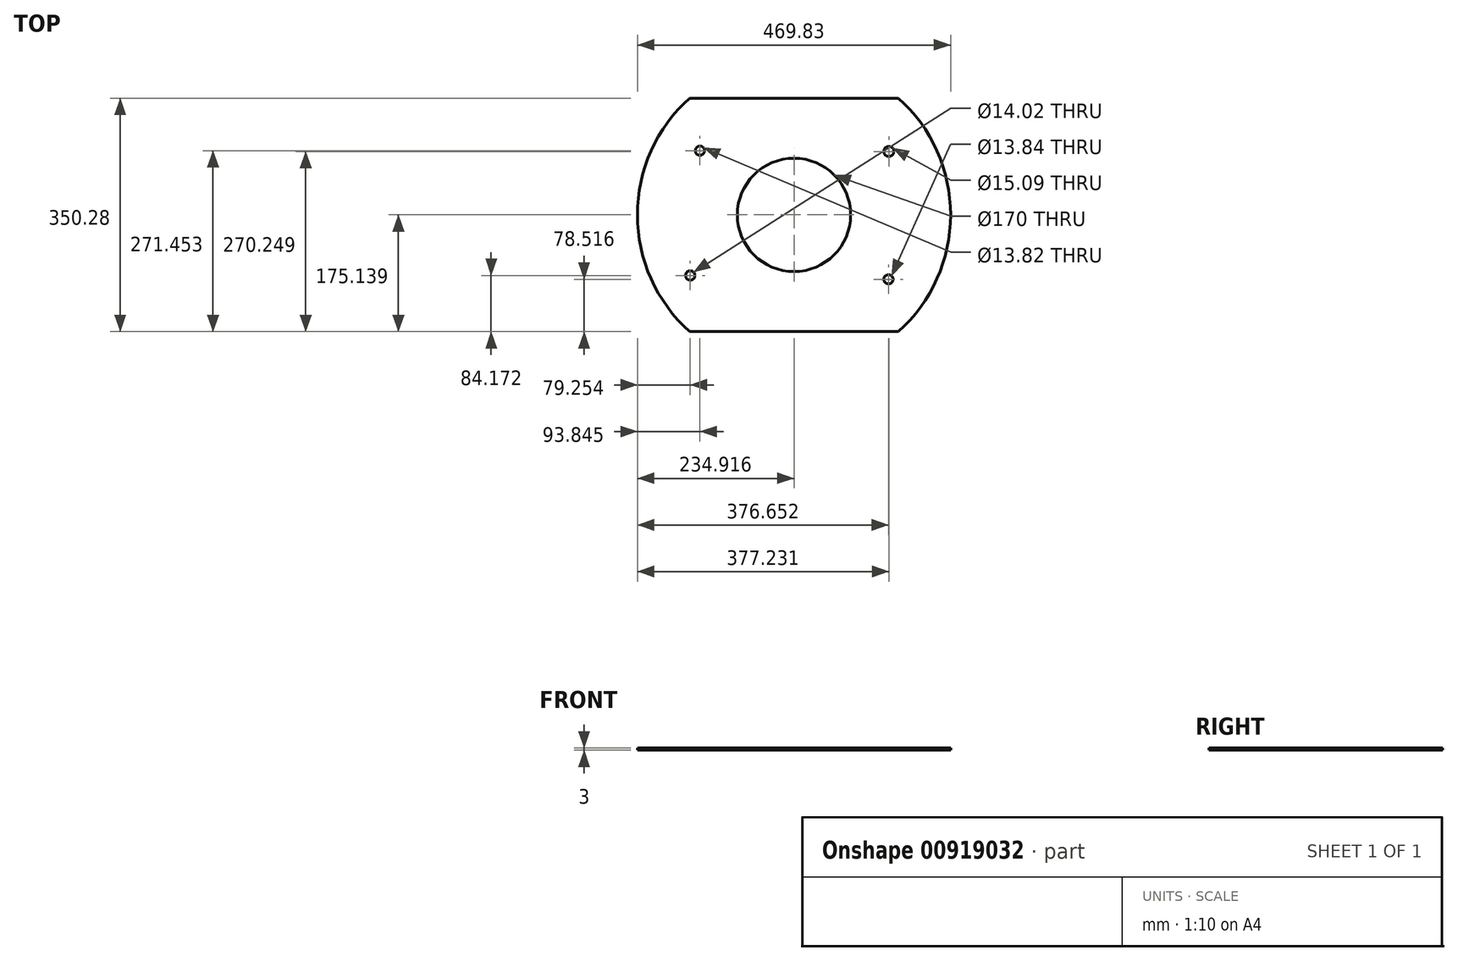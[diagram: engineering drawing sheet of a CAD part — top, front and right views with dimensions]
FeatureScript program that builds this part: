
annotation { "Feature Type Name" : "Feature", "Feature Type Description" : "" }
export const myFeature = defineFeature(function(context is Context, id is Id, definition is map)
    precondition{}
    {
        {
            var Q0;
            Q0=qCreatedBy(makeId("Top.planeOp"),FACE);
            var sketch = newSketch(context, id + "F0", { "sketchPlane" : qUnion([Q0])});
            skLineSegment(sketch, "E0", {"start": v(-158.77, -147.96) * mm, "end": v(-154.5, -152.35) * mm});
            skLineSegment(sketch, "E1", {"start": v(-154.5, -152.35) * mm, "end": v(-152.51, -152.53) * mm});
            skLineSegment(sketch, "E2", {"start": v(151.5, -153.31) * mm, "end": v(154.39, -153.06) * mm});
            skLineSegment(sketch, "E3", {"start": v(154.39, -153.06) * mm, "end": v(158.17, -149.2) * mm});
            skLineSegment(sketch, "E4", {"start": v(158.99, -149.86) * mm, "end": v(155.02, -154) * mm});
            skLineSegment(sketch, "E5", {"start": v(155.02, -154) * mm, "end": v(122.13, -154) * mm});
            skLineSegment(sketch, "E6", {"start": v(44.59, -153.79) * mm, "end": v(44.59, -153.79) * mm});
            skLineSegment(sketch, "E7", {"start": v(-66.83, -70.4) * mm, "end": v(-66.83, -55.46) * mm});
            skLineSegment(sketch, "E8", {"start": v(-66.83, -55.46) * mm, "end": v(-68.23, -53.8) * mm});
            skLineSegment(sketch, "E9", {"start": v(-69.12, 57.2) * mm, "end": v(-66.84, 60.02) * mm});
            skLineSegment(sketch, "E10", {"start": v(-66.84, 60.02) * mm, "end": v(-66.66, 75.23) * mm});
            skLineSegment(sketch, "E11", {"start": v(67.44, 72.4) * mm, "end": v(67.45, 59.42) * mm});
            skLineSegment(sketch, "E12", {"start": v(67.45, 59.42) * mm, "end": v(68.38, 58.55) * mm});
            skLineSegment(sketch, "E13", {"start": v(69.37, -52.77) * mm, "end": v(67.06, -55.7) * mm});
            skLineSegment(sketch, "E14", {"start": v(67.06, -55.7) * mm, "end": v(67.1, -70.3) * mm});
            skLineSegment(sketch, "E15", {"start": v(-48.47, -97.3) * mm, "end": v(-48.47, -97.3) * mm});
            skLineSegment(sketch, "E16", {"start": v(67.43, 58.04) * mm, "end": v(66.42, 59.12) * mm});
            skLineSegment(sketch, "E17", {"start": v(66.42, 59.12) * mm, "end": v(66.3, 74.42) * mm});
            skLineSegment(sketch, "E18", {"start": v(66.3, 74.42) * mm, "end": v(66.19, 89.72) * mm});
            skLineSegment(sketch, "E19", {"start": v(66.19, 89.72) * mm, "end": v(65.15, 91.97) * mm});
            skLineSegment(sketch, "E20", {"start": v(-65.75, 73.8) * mm, "end": v(-65.75, 59.65) * mm});
            skLineSegment(sketch, "E21", {"start": v(-65.75, 59.65) * mm, "end": v(-67.84, 57.04) * mm});
            skLineSegment(sketch, "E22", {"start": v(-159.56, -89.44) * mm, "end": v(-158.1, -89.5) * mm});
            skLineSegment(sketch, "E23", {"start": v(-158.1, -89.5) * mm, "end": v(-159.71, -89.73) * mm});
            skFitSpline(sketch, "E24", {"points": [v(44.59, -153.79) * mm, v(20.04, -153.67) * mm, v(-34.6, -153.55) * mm, v(-76.83, -153.52) * mm]});
            skFitSpline(sketch, "E25", {"points": [v(-76.83, -153.52) * mm, v(-140.66, -153.47) * mm, v(-153.81, -153.38) * mm, v(-154.79, -152.98) * mm]});
            skFitSpline(sketch, "E26", {"points": [v(-154.79, -152.98) * mm, v(-155.87, -152.52) * mm, v(-163.77, -144.52) * mm, v(-166.1, -141.52) * mm]});
            skFitSpline(sketch, "E27", {"points": [v(-166.1, -141.52) * mm, v(-166.64, -140.82) * mm, v(-168.72, -138.23) * mm, v(-170.71, -135.78) * mm]});
            skFitSpline(sketch, "E28", {"points": [v(-170.71, -135.78) * mm, v(-179.67, -124.75) * mm, v(-185.63, -115.93) * mm, v(-192.42, -103.68) * mm]});
            skFitSpline(sketch, "E29", {"points": [v(-192.42, -103.68) * mm, v(-204.28, -82.26) * mm, v(-211.62, -61.65) * mm, v(-216.38, -36.46) * mm]});
            skFitSpline(sketch, "E30", {"points": [v(-216.38, -36.46) * mm, v(-217.29, -31.66) * mm, v(-217.57, -29.6) * mm, v(-218.57, -20.44) * mm]});
            skFitSpline(sketch, "E31", {"points": [v(-218.57, -20.44) * mm, v(-220.9, 0.8) * mm, v(-219.77, 25.42) * mm, v(-215.48, 46.88) * mm]});
            skFitSpline(sketch, "E32", {"points": [v(-215.48, 46.88) * mm, v(-212.67, 60.96) * mm, v(-207.35, 77.93) * mm, v(-202.01, 89.9) * mm]});
            skFitSpline(sketch, "E33", {"points": [v(-202.01, 89.9) * mm, v(-201.35, 91.38) * mm, v(-200.41, 93.49) * mm, v(-199.93, 94.58) * mm]});
            skFitSpline(sketch, "E34", {"points": [v(-199.93, 94.58) * mm, v(-195.35, 104.83) * mm, v(-187.95, 117.86) * mm, v(-181.24, 127.48) * mm]});
            skFitSpline(sketch, "E35", {"points": [v(-181.24, 127.48) * mm, v(-179.6, 129.84) * mm, v(-177.74, 132.5) * mm, v(-177.1, 133.42) * mm]});
            skFitSpline(sketch, "E36", {"points": [v(-177.1, 133.42) * mm, v(-176.48, 134.33) * mm, v(-175.76, 135.3) * mm, v(-175.51, 135.58) * mm]});
            skFitSpline(sketch, "E37", {"points": [v(-175.51, 135.58) * mm, v(-175.26, 135.86) * mm, v(-173.96, 137.54) * mm, v(-172.6, 139.33) * mm]});
            skFitSpline(sketch, "E38", {"points": [v(-172.6, 139.33) * mm, v(-171.26, 141.1) * mm, v(-169.83, 142.8) * mm, v(-169.43, 143.07) * mm]});
            skFitSpline(sketch, "E39", {"points": [v(-169.43, 143.07) * mm, v(-168.68, 143.6) * mm, v(-168.4, 144.5) * mm, v(-169.13, 144.04) * mm]});
            skFitSpline(sketch, "E40", {"points": [v(-169.13, 144.04) * mm, v(-169.39, 143.88) * mm, v(-169.44, 143.94) * mm, v(-169.28, 144.2) * mm]});
            skFitSpline(sketch, "E41", {"points": [v(-169.28, 144.2) * mm, v(-169.14, 144.44) * mm, v(-168.88, 144.54) * mm, v(-168.7, 144.43) * mm]});
            skFitSpline(sketch, "E42", {"points": [v(-168.7, 144.43) * mm, v(-168.53, 144.32) * mm, v(-168.1, 144.68) * mm, v(-167.75, 145.23) * mm]});
            skFitSpline(sketch, "E43", {"points": [v(-167.75, 145.23) * mm, v(-166.97, 146.48) * mm, v(-166.35, 147.22) * mm, v(-164.75, 148.82) * mm]});
            skFitSpline(sketch, "E44", {"points": [v(-164.75, 148.82) * mm, v(-164.06, 149.5) * mm, v(-163.53, 150.23) * mm, v(-163.59, 150.43) * mm]});
            skFitSpline(sketch, "E45", {"points": [v(-163.59, 150.43) * mm, v(-163.64, 150.63) * mm, v(-163.53, 150.7) * mm, v(-163.33, 150.57) * mm]});
            skFitSpline(sketch, "E46", {"points": [v(-163.33, 150.57) * mm, v(-163.14, 150.45) * mm, v(-162.37, 151.17) * mm, v(-161.63, 152.16) * mm]});
            skFitSpline(sketch, "E47", {"points": [v(-161.63, 152.16) * mm, v(-160.68, 153.44) * mm, v(-160.03, 153.98) * mm, v(-159.43, 153.98) * mm]});
            skFitSpline(sketch, "E48", {"points": [v(-159.43, 153.98) * mm, v(-158.36, 153.98) * mm, v(-158.43, 153.86) * mm, v(-161.98, 150.14) * mm]});
            skFitSpline(sketch, "E49", {"points": [v(-161.98, 150.14) * mm, v(-163.58, 148.46) * mm, v(-165.14, 146.73) * mm, v(-165.44, 146.3) * mm]});
            skFitSpline(sketch, "E50", {"points": [v(-165.44, 146.3) * mm, v(-165.73, 145.87) * mm, v(-167.52, 143.65) * mm, v(-169.41, 141.37) * mm]});
            skFitSpline(sketch, "E51", {"points": [v(-169.41, 141.37) * mm, v(-171.3, 139.1) * mm, v(-173.57, 136.26) * mm, v(-174.46, 135.07) * mm]});
            skFitSpline(sketch, "E52", {"points": [v(-174.46, 135.07) * mm, v(-175.34, 133.89) * mm, v(-176.2, 132.75) * mm, v(-176.35, 132.56) * mm]});
            skFitSpline(sketch, "E53", {"points": [v(-176.35, 132.56) * mm, v(-178.97, 129.3) * mm, v(-186.94, 116.97) * mm, v(-191.22, 109.52) * mm]});
            skFitSpline(sketch, "E54", {"points": [v(-191.22, 109.52) * mm, v(-202.62, 89.66) * mm, v(-211.97, 63.16) * mm, v(-215.86, 39.68) * mm]});
            skFitSpline(sketch, "E55", {"points": [v(-215.86, 39.68) * mm, v(-219.82, 15.76) * mm, v(-219.68, -14.45) * mm, v(-215.5, -35.92) * mm]});
            skFitSpline(sketch, "E56", {"points": [v(-215.5, -35.92) * mm, v(-215.35, -36.72) * mm, v(-214.97, -38.74) * mm, v(-214.66, -40.42) * mm]});
            skFitSpline(sketch, "E57", {"points": [v(-214.66, -40.42) * mm, v(-212.88, -50) * mm, v(-207.62, -67.85) * mm, v(-203.63, -77.86) * mm]});
            skFitSpline(sketch, "E58", {"points": [v(-203.63, -77.86) * mm, v(-196.86, -94.81) * mm, v(-186.42, -113.45) * mm, v(-175.6, -127.9) * mm]});
            skFitSpline(sketch, "E59", {"points": [v(-175.6, -127.9) * mm, v(-170.94, -134.11) * mm, v(-162.77, -143.86) * mm, v(-158.77, -147.96) * mm]});
            skFitSpline(sketch, "E60", {"points": [v(-152.51, -152.53) * mm, v(-151.42, -152.63) * mm, v(-87.6, -152.8) * mm, v(-10.67, -152.91) * mm]});
            skFitSpline(sketch, "E61", {"points": [v(-10.67, -152.91) * mm, v(66.25, -153.02) * mm, v(133.56, -153.21) * mm, v(138.9, -153.34) * mm]});
            skFitSpline(sketch, "E62", {"points": [v(138.9, -153.34) * mm, v(144.26, -153.47) * mm, v(149.93, -153.46) * mm, v(151.5, -153.31) * mm]});
            skFitSpline(sketch, "E63", {"points": [v(158.17, -149.2) * mm, v(171.85, -135.25) * mm, v(186.95, -114) * mm, v(195.38, -96.84) * mm]});
            skFitSpline(sketch, "E64", {"points": [v(195.38, -96.84) * mm, v(206.59, -74.03) * mm, v(213.5, -52.17) * mm, v(216.67, -29.5) * mm]});
            skFitSpline(sketch, "E65", {"points": [v(216.67, -29.5) * mm, v(218.46, -16.68) * mm, v(218.78, -11.86) * mm, v(218.8, 2.42) * mm]});
            skFitSpline(sketch, "E66", {"points": [v(218.8, 2.42) * mm, v(218.81, 12.95) * mm, v(218.68, 17.26) * mm, v(218.17, 22.04) * mm]});
            skFitSpline(sketch, "E67", {"points": [v(218.17, 22.04) * mm, v(216.47, 38.25) * mm, v(213.8, 51.98) * mm, v(209.83, 65.05) * mm]});
            skFitSpline(sketch, "E68", {"points": [v(209.83, 65.05) * mm, v(208.18, 70.46) * mm, v(205.5, 78.4) * mm, v(204.97, 79.42) * mm]});
            skFitSpline(sketch, "E69", {"points": [v(204.97, 79.42) * mm, v(204.8, 79.73) * mm, v(204.4, 80.8) * mm, v(204.05, 81.8) * mm]});
            skFitSpline(sketch, "E70", {"points": [v(204.05, 81.8) * mm, v(203.7, 82.79) * mm, v(202.88, 84.78) * mm, v(202.22, 86.23) * mm]});
            skFitSpline(sketch, "E71", {"points": [v(202.22, 86.23) * mm, v(201.55, 87.68) * mm, v(201, 88.95) * mm, v(201, 89.06) * mm]});
            skFitSpline(sketch, "E72", {"points": [v(201, 89.06) * mm, v(201, 89.32) * mm, v(197.35, 97.26) * mm, v(195.3, 101.42) * mm]});
            skFitSpline(sketch, "E73", {"points": [v(195.3, 101.42) * mm, v(193.27, 105.57) * mm, v(188.66, 113.76) * mm, v(187.47, 115.34) * mm]});
            skFitSpline(sketch, "E74", {"points": [v(187.47, 115.34) * mm, v(187, 115.97) * mm, v(186.6, 116.57) * mm, v(186.6, 116.68) * mm]});
            skFitSpline(sketch, "E75", {"points": [v(186.6, 116.68) * mm, v(186.6, 117.07) * mm, v(182.91, 122.72) * mm, v(178.41, 129.2) * mm]});
            skFitSpline(sketch, "E76", {"points": [v(178.41, 129.2) * mm, v(173.94, 135.64) * mm, v(164.9, 146.79) * mm, v(161.08, 150.55) * mm]});
            skFitSpline(sketch, "E77", {"points": [v(161.08, 150.55) * mm, v(159.48, 152.13) * mm, v(158.17, 153.54) * mm, v(158.17, 153.7) * mm]});
            skFitSpline(sketch, "E78", {"points": [v(158.17, 153.7) * mm, v(158.17, 154.35) * mm, v(159.74, 153.9) * mm, v(160.65, 152.99) * mm]});
            skFitSpline(sketch, "E79", {"points": [v(160.65, 152.99) * mm, v(163.2, 150.41) * mm, v(166.83, 146.25) * mm, v(170.34, 141.9) * mm]});
            skFitSpline(sketch, "E80", {"points": [v(170.34, 141.9) * mm, v(176.5, 134.25) * mm, v(177.44, 133.03) * mm, v(178.79, 130.92) * mm]});
            skFitSpline(sketch, "E81", {"points": [v(178.79, 130.92) * mm, v(179.49, 129.82) * mm, v(180.32, 128.7) * mm, v(180.63, 128.45) * mm]});
            skFitSpline(sketch, "E82", {"points": [v(180.63, 128.45) * mm, v(180.95, 128.18) * mm, v(181.2, 127.81) * mm, v(181.2, 127.62) * mm]});
            skFitSpline(sketch, "E83", {"points": [v(181.2, 127.62) * mm, v(181.2, 127.43) * mm, v(181.78, 126.51) * mm, v(182.48, 125.6) * mm]});
            skFitSpline(sketch, "E84", {"points": [v(182.48, 125.6) * mm, v(183.98, 123.61) * mm, v(188.05, 117.4) * mm, v(188.05, 117.08) * mm]});
            skFitSpline(sketch, "E85", {"points": [v(188.05, 117.08) * mm, v(188.05, 116.96) * mm, v(188.72, 115.86) * mm, v(189.54, 114.63) * mm]});
            skFitSpline(sketch, "E86", {"points": [v(189.54, 114.63) * mm, v(191.13, 112.24) * mm, v(196.77, 101.25) * mm, v(198.83, 96.53) * mm]});
            skFitSpline(sketch, "E87", {"points": [v(198.83, 96.53) * mm, v(199.52, 94.96) * mm, v(200.75, 92.22) * mm, v(201.56, 90.44) * mm]});
            skFitSpline(sketch, "E88", {"points": [v(201.56, 90.44) * mm, v(202.38, 88.65) * mm, v(203.34, 86.47) * mm, v(203.7, 85.58) * mm]});
            skFitSpline(sketch, "E89", {"points": [v(203.7, 85.58) * mm, v(204.06, 84.68) * mm, v(204.57, 83.44) * mm, v(204.84, 82.82) * mm]});
            skFitSpline(sketch, "E90", {"points": [v(204.84, 82.82) * mm, v(205.1, 82.2) * mm, v(205.33, 81.46) * mm, v(205.33, 81.18) * mm]});
            skFitSpline(sketch, "E91", {"points": [v(205.33, 81.18) * mm, v(205.33, 80.9) * mm, v(205.48, 80.53) * mm, v(205.66, 80.34) * mm]});
            skFitSpline(sketch, "E92", {"points": [v(205.66, 80.34) * mm, v(205.83, 80.15) * mm, v(206.88, 77.32) * mm, v(207.98, 74.06) * mm]});
            skFitSpline(sketch, "E93", {"points": [v(207.98, 74.06) * mm, v(214.3, 55.25) * mm, v(217.55, 39.5) * mm, v(219.38, 18.8) * mm]});
            skFitSpline(sketch, "E94", {"points": [v(219.38, 18.8) * mm, v(219.87, 13.33) * mm, v(219.87, -6.17) * mm, v(219.39, -13.14) * mm]});
            skFitSpline(sketch, "E95", {"points": [v(219.39, -13.14) * mm, v(217.23, -44.28) * mm, v(208.41, -74.87) * mm, v(193.73, -102.16) * mm]});
            skFitSpline(sketch, "E96", {"points": [v(193.73, -102.16) * mm, v(184.56, -119.22) * mm, v(172.55, -135.71) * mm, v(158.99, -149.86) * mm]});
            skFitSpline(sketch, "E97", {"points": [v(122.13, -154) * mm, v(104.03, -154) * mm, v(69.14, -153.9) * mm, v(44.59, -153.79) * mm]});
            skFitSpline(sketch, "E98", {"points": [v(-132.8, -152.15) * mm, v(-132.56, -152.05) * mm, v(-132.08, -152.04) * mm, v(-131.73, -152.14) * mm]});
            skFitSpline(sketch, "E99", {"points": [v(-131.73, -152.14) * mm, v(-131.38, -152.23) * mm, v(-131.58, -152.3) * mm, v(-132.17, -152.31) * mm]});
            skFitSpline(sketch, "E100", {"points": [v(-132.17, -152.31) * mm, v(-132.76, -152.32) * mm, v(-133.05, -152.25) * mm, v(-132.8, -152.15) * mm]});
            skFitSpline(sketch, "E101", {"points": [v(142.69, -101.62) * mm, v(142.69, -101.1) * mm, v(142.93, -100.9) * mm, v(143.6, -100.9) * mm]});
            skFitSpline(sketch, "E102", {"points": [v(143.6, -100.9) * mm, v(144.1, -100.9) * mm, v(145.39, -100.4) * mm, v(146.48, -99.8) * mm]});
            skFitSpline(sketch, "E103", {"points": [v(146.48, -99.8) * mm, v(147.56, -99.18) * mm, v(148.45, -98.85) * mm, v(148.45, -99.06) * mm]});
            skFitSpline(sketch, "E104", {"points": [v(148.45, -99.06) * mm, v(148.45, -99.56) * mm, v(145.11, -101.26) * mm, v(144.14, -101.26) * mm]});
            skFitSpline(sketch, "E105", {"points": [v(144.14, -101.26) * mm, v(143.74, -101.26) * mm, v(143.4, -101.43) * mm, v(143.4, -101.62) * mm]});
            skFitSpline(sketch, "E106", {"points": [v(143.4, -101.62) * mm, v(143.4, -102.28) * mm, v(144.55, -102) * mm, v(146.52, -100.88) * mm]});
            skFitSpline(sketch, "E107", {"points": [v(146.52, -100.88) * mm, v(147.59, -100.27) * mm, v(148.66, -99.83) * mm, v(148.9, -99.92) * mm]});
            skFitSpline(sketch, "E108", {"points": [v(148.9, -99.92) * mm, v(149.15, -100) * mm, v(148.46, -100.58) * mm, v(147.37, -101.2) * mm]});
            skFitSpline(sketch, "E109", {"points": [v(147.37, -101.2) * mm, v(144.98, -102.57) * mm, v(142.69, -102.78) * mm, v(142.69, -101.62) * mm]});
            skFitSpline(sketch, "E110", {"points": [v(137.6, -98.15) * mm, v(133.77, -97.67) * mm, v(133.36, -91.62) * mm, v(136.96, -88.54) * mm]});
            skFitSpline(sketch, "E111", {"points": [v(136.96, -88.54) * mm, v(137.73, -87.88) * mm, v(138.37, -87.07) * mm, v(138.37, -86.74) * mm]});
            skFitSpline(sketch, "E112", {"points": [v(138.37, -86.74) * mm, v(138.37, -86.38) * mm, v(138.66, -86.14) * mm, v(139.09, -86.14) * mm]});
            skFitSpline(sketch, "E113", {"points": [v(139.09, -86.14) * mm, v(139.49, -86.14) * mm, v(139.8, -86.35) * mm, v(139.8, -86.6) * mm]});
            skFitSpline(sketch, "E114", {"points": [v(139.8, -86.6) * mm, v(139.8, -86.92) * mm, v(140.25, -87.02) * mm, v(141.23, -86.93) * mm]});
            skFitSpline(sketch, "E115", {"points": [v(141.23, -86.93) * mm, v(144.18, -86.65) * mm, v(147.72, -88.89) * mm, v(148.44, -91.5) * mm]});
            skFitSpline(sketch, "E116", {"points": [v(148.44, -91.5) * mm, v(149.2, -94.2) * mm, v(148.6, -97.25) * mm, v(147.23, -97.78) * mm]});
            skFitSpline(sketch, "E117", {"points": [v(147.23, -97.78) * mm, v(146.49, -98.06) * mm, v(139.18, -98.34) * mm, v(137.6, -98.15) * mm]});
            skFitSpline(sketch, "E118", {"points": [v(145.66, -96.8) * mm, v(145.85, -96.52) * mm, v(146.02, -96.55) * mm, v(146.24, -96.9) * mm]});
            skFitSpline(sketch, "E119", {"points": [v(146.24, -96.9) * mm, v(146.83, -97.8) * mm, v(147.49, -95.95) * mm, v(147.52, -93.32) * mm]});
            skFitSpline(sketch, "E120", {"points": [v(147.52, -93.32) * mm, v(147.58, -89.34) * mm, v(143.1, -86.76) * mm, v(139.05, -88.45) * mm]});
            skFitSpline(sketch, "E121", {"points": [v(139.05, -88.45) * mm, v(137.66, -89.03) * mm, v(136.92, -89.77) * mm, v(136.08, -91.42) * mm]});
            skFitSpline(sketch, "E122", {"points": [v(136.08, -91.42) * mm, v(135.5, -92.59) * mm, v(135.37, -95.14) * mm, v(135.9, -95.14) * mm]});
            skFitSpline(sketch, "E123", {"points": [v(135.9, -95.14) * mm, v(136.07, -95.14) * mm, v(136.2, -95.54) * mm, v(136.2, -96.02) * mm]});
            skFitSpline(sketch, "E124", {"points": [v(136.2, -96.02) * mm, v(136.2, -96.5) * mm, v(136.37, -97) * mm, v(136.57, -97.12) * mm]});
            skFitSpline(sketch, "E125", {"points": [v(136.57, -97.12) * mm, v(136.77, -97.25) * mm, v(136.93, -97.06) * mm, v(136.93, -96.72) * mm]});
            skFitSpline(sketch, "E126", {"points": [v(136.93, -96.72) * mm, v(136.93, -96.13) * mm, v(136.97, -96.14) * mm, v(137.42, -96.75) * mm]});
            skFitSpline(sketch, "E127", {"points": [v(137.42, -96.75) * mm, v(137.68, -97.12) * mm, v(138.05, -97.32) * mm, v(138.23, -97.2) * mm]});
            skFitSpline(sketch, "E128", {"points": [v(138.23, -97.2) * mm, v(138.42, -97.1) * mm, v(139.13, -97.12) * mm, v(139.82, -97.26) * mm]});
            skFitSpline(sketch, "E129", {"points": [v(139.82, -97.26) * mm, v(141.5, -97.6) * mm, v(145.32, -97.3) * mm, v(145.66, -96.8) * mm]});
            skFitSpline(sketch, "E130", {"points": [v(-48.47, -97.3) * mm, v(-56.8, -96.95) * mm, v(-59.86, -96.3) * mm, v(-61.86, -94.5) * mm]});
            skFitSpline(sketch, "E131", {"points": [v(-61.86, -94.5) * mm, v(-63.94, -92.62) * mm, v(-65.2, -90.6) * mm, v(-66.07, -87.81) * mm]});
            skFitSpline(sketch, "E132", {"points": [v(-66.07, -87.81) * mm, v(-66.8, -85.47) * mm, v(-66.83, -84.6) * mm, v(-66.83, -70.4) * mm]});
            skFitSpline(sketch, "E133", {"points": [v(-68.23, -53.8) * mm, v(-81.54, -37.86) * mm, v(-89.18, -15.51) * mm, v(-88.3, 4.94) * mm]});
            skFitSpline(sketch, "E134", {"points": [v(-88.3, 4.94) * mm, v(-87.46, 24.43) * mm, v(-80.7, 42.86) * mm, v(-69.12, 57.2) * mm]});
            skFitSpline(sketch, "E135", {"points": [v(-66.66, 75.23) * mm, v(-66.52, 87.88) * mm, v(-66.4, 90.77) * mm, v(-65.9, 92.42) * mm]});
            skFitSpline(sketch, "E136", {"points": [v(-65.9, 92.42) * mm, v(-64.15, 98.32) * mm, v(-59.37, 102.95) * mm, v(-53.7, 104.25) * mm]});
            skFitSpline(sketch, "E137", {"points": [v(-53.7, 104.25) * mm, v(-51.2, 104.82) * mm, v(-52.44, 104.8) * mm, v(2.1, 104.72) * mm]});
            skFitSpline(sketch, "E138", {"points": [v(2.1, 104.72) * mm, v(55.94, 104.63) * mm, v(53.66, 104.72) * mm, v(57.72, 102.43) * mm]});
            skFitSpline(sketch, "E139", {"points": [v(57.72, 102.43) * mm, v(60.55, 100.83) * mm, v(63.19, 98.75) * mm, v(64.11, 97.36) * mm]});
            skFitSpline(sketch, "E140", {"points": [v(64.11, 97.36) * mm, v(65.6, 95.16) * mm, v(66.78, 91.65) * mm, v(67.11, 88.48) * mm]});
            skFitSpline(sketch, "E141", {"points": [v(67.11, 88.48) * mm, v(67.3, 86.78) * mm, v(67.44, 79.55) * mm, v(67.44, 72.4) * mm]});
            skFitSpline(sketch, "E142", {"points": [v(68.38, 58.55) * mm, v(68.9, 58.07) * mm, v(70.4, 56.14) * mm, v(71.73, 54.26) * mm]});
            skFitSpline(sketch, "E143", {"points": [v(71.73, 54.26) * mm, v(82.98, 38.3) * mm, v(88.44, 21.38) * mm, v(88.42, 2.6) * mm]});
            skFitSpline(sketch, "E144", {"points": [v(88.42, 2.6) * mm, v(88.41, -7.6) * mm, v(87.29, -15.27) * mm, v(84.53, -23.86) * mm]});
            skFitSpline(sketch, "E145", {"points": [v(84.53, -23.86) * mm, v(83.8, -26.14) * mm, v(82.97, -28.76) * mm, v(82.69, -29.69) * mm]});
            skFitSpline(sketch, "E146", {"points": [v(82.69, -29.69) * mm, v(81.79, -32.63) * mm, v(76.92, -42.04) * mm, v(74.25, -46) * mm]});
            skFitSpline(sketch, "E147", {"points": [v(74.25, -46) * mm, v(72.84, -48.1) * mm, v(70.64, -51.15) * mm, v(69.37, -52.77) * mm]});
            skFitSpline(sketch, "E148", {"points": [v(67.1, -70.3) * mm, v(67.13, -79.3) * mm, v(67.01, -85.5) * mm, v(66.78, -86.5) * mm]});
            skFitSpline(sketch, "E149", {"points": [v(66.78, -86.5) * mm, v(65.94, -90.15) * mm, v(63.73, -93.8) * mm, v(61.31, -95.52) * mm]});
            skFitSpline(sketch, "E150", {"points": [v(61.31, -95.52) * mm, v(58.68, -97.4) * mm, v(58.16, -97.41) * mm, v(6.25, -97.5) * mm]});
            skFitSpline(sketch, "E151", {"points": [v(6.25, -97.5) * mm, v(-20.18, -97.53) * mm, v(-44.8, -97.44) * mm, v(-48.47, -97.3) * mm]});
            skFitSpline(sketch, "E152", {"points": [v(50.61, -95.73) * mm, v(52.34, -95.61) * mm, v(54.09, -95.31) * mm, v(54.5, -95.06) * mm]});
            skFitSpline(sketch, "E153", {"points": [v(54.5, -95.06) * mm, v(55.1, -94.68) * mm, v(55.29, -94.7) * mm, v(55.58, -95.14) * mm]});
            skFitSpline(sketch, "E154", {"points": [v(55.58, -95.14) * mm, v(55.87, -95.6) * mm, v(55.92, -95.6) * mm, v(55.92, -95.05) * mm]});
            skFitSpline(sketch, "E155", {"points": [v(55.92, -95.05) * mm, v(55.93, -94.57) * mm, v(56.23, -94.42) * mm, v(57.23, -94.42) * mm]});
            skFitSpline(sketch, "E156", {"points": [v(57.23, -94.42) * mm, v(58.35, -94.42) * mm, v(58.47, -94.5) * mm, v(58.09, -94.96) * mm]});
            skFitSpline(sketch, "E157", {"points": [v(58.09, -94.96) * mm, v(57.39, -95.81) * mm, v(58.55, -95.67) * mm, v(59.33, -94.8) * mm]});
            skFitSpline(sketch, "E158", {"points": [v(59.33, -94.8) * mm, v(59.67, -94.43) * mm, v(60.17, -94.2) * mm, v(60.44, -94.3) * mm]});
            skFitSpline(sketch, "E159", {"points": [v(60.44, -94.3) * mm, v(60.7, -94.4) * mm, v(61.2, -94.03) * mm, v(61.57, -93.46) * mm]});
            skFitSpline(sketch, "E160", {"points": [v(61.57, -93.46) * mm, v(61.93, -92.9) * mm, v(62.65, -92.09) * mm, v(63.17, -91.65) * mm]});
            skFitSpline(sketch, "E161", {"points": [v(63.17, -91.65) * mm, v(64.21, -90.76) * mm, v(65.92, -86.36) * mm, v(66, -84.34) * mm]});
            skFitSpline(sketch, "E162", {"points": [v(66, -84.34) * mm, v(66.03, -83.65) * mm, v(66.14, -76.6) * mm, v(66.24, -68.68) * mm]});
            skFitSpline(sketch, "E163", {"points": [v(66.24, -68.68) * mm, v(66.4, -56.92) * mm, v(66.52, -54.18) * mm, v(66.94, -53.72) * mm]});
            skFitSpline(sketch, "E164", {"points": [v(66.94, -53.72) * mm, v(67.22, -53.4) * mm, v(67.45, -53) * mm, v(67.45, -52.81) * mm]});
            skFitSpline(sketch, "E165", {"points": [v(67.45, -52.81) * mm, v(67.45, -52.63) * mm, v(68.17, -51.67) * mm, v(69.06, -50.68) * mm]});
            skFitSpline(sketch, "E166", {"points": [v(69.06, -50.68) * mm, v(69.94, -49.7) * mm, v(70.87, -48.48) * mm, v(71.13, -47.98) * mm]});
            skFitSpline(sketch, "E167", {"points": [v(71.13, -47.98) * mm, v(71.38, -47.49) * mm, v(71.96, -46.68) * mm, v(72.42, -46.18) * mm]});
            skFitSpline(sketch, "E168", {"points": [v(72.42, -46.18) * mm, v(72.87, -45.69) * mm, v(73.53, -44.8) * mm, v(73.89, -44.2) * mm]});
            skFitSpline(sketch, "E169", {"points": [v(73.89, -44.2) * mm, v(75.84, -40.94) * mm, v(76.6, -39.49) * mm, v(76.5, -39.18) * mm]});
            skFitSpline(sketch, "E170", {"points": [v(76.5, -39.18) * mm, v(76.45, -38.99) * mm, v(76.62, -38.66) * mm, v(76.89, -38.46) * mm]});
            skFitSpline(sketch, "E171", {"points": [v(76.89, -38.46) * mm, v(77.36, -38.1) * mm, v(78.17, -36.52) * mm, v(80.23, -31.96) * mm]});
            skFitSpline(sketch, "E172", {"points": [v(80.23, -31.96) * mm, v(80.77, -30.78) * mm, v(81.36, -29.51) * mm, v(81.54, -29.16) * mm]});
            skFitSpline(sketch, "E173", {"points": [v(81.54, -29.16) * mm, v(81.72, -28.8) * mm, v(81.78, -28.36) * mm, v(81.66, -28.17) * mm]});
            skFitSpline(sketch, "E174", {"points": [v(81.66, -28.17) * mm, v(81.54, -27.98) * mm, v(81.6, -27.82) * mm, v(81.79, -27.82) * mm]});
            skFitSpline(sketch, "E175", {"points": [v(81.79, -27.82) * mm, v(81.97, -27.82) * mm, v(82.21, -27.54) * mm, v(82.32, -27.2) * mm]});
            skFitSpline(sketch, "E176", {"points": [v(82.32, -27.2) * mm, v(82.42, -26.85) * mm, v(82.85, -25.63) * mm, v(83.26, -24.49) * mm]});
            skFitSpline(sketch, "E177", {"points": [v(83.26, -24.49) * mm, v(85.66, -17.9) * mm, v(87.2, -9.1) * mm, v(87.5, -0.1) * mm]});
            skFitSpline(sketch, "E178", {"points": [v(87.5, -0.1) * mm, v(88.13, 19.1) * mm, v(82.14, 38.18) * mm, v(70.4, 54.26) * mm]});
            skFitSpline(sketch, "E179", {"points": [v(70.4, 54.26) * mm, v(69.32, 55.74) * mm, v(67.98, 57.44) * mm, v(67.43, 58.04) * mm]});
            skFitSpline(sketch, "E180", {"points": [v(65.15, 91.97) * mm, v(64.58, 93.2) * mm, v(64, 94.22) * mm, v(63.87, 94.22) * mm]});
            skFitSpline(sketch, "E181", {"points": [v(63.87, 94.22) * mm, v(63.73, 94.22) * mm, v(63.36, 94.74) * mm, v(63.05, 95.39) * mm]});
            skFitSpline(sketch, "E182", {"points": [v(63.05, 95.39) * mm, v(60.89, 99.78) * mm, v(55.01, 103.45) * mm, v(49.9, 103.59) * mm]});
            skFitSpline(sketch, "E183", {"points": [v(49.9, 103.59) * mm, v(48.77, 103.62) * mm, v(32.28, 103.63) * mm, v(13.27, 103.6) * mm]});
            skFitSpline(sketch, "E184", {"points": [v(13.27, 103.6) * mm, v(-5.74, 103.58) * mm, v(-27.53, 103.67) * mm, v(-35.15, 103.8) * mm]});
            skFitSpline(sketch, "E185", {"points": [v(-35.15, 103.8) * mm, v(-45.07, 103.97) * mm, v(-49.77, 103.91) * mm, v(-51.7, 103.6) * mm]});
            skFitSpline(sketch, "E186", {"points": [v(-51.7, 103.6) * mm, v(-54.47, 103.17) * mm, v(-58.03, 101.65) * mm, v(-59.63, 100.22) * mm]});
            skFitSpline(sketch, "E187", {"points": [v(-59.63, 100.22) * mm, v(-61.27, 98.76) * mm, v(-62.89, 96.7) * mm, v(-62.68, 96.35) * mm]});
            skFitSpline(sketch, "E188", {"points": [v(-62.68, 96.35) * mm, v(-62.56, 96.17) * mm, v(-62.63, 96.02) * mm, v(-62.84, 96.02) * mm]});
            skFitSpline(sketch, "E189", {"points": [v(-62.84, 96.02) * mm, v(-63.4, 96.02) * mm, v(-64.93, 92.42) * mm, v(-65.36, 90.06) * mm]});
            skFitSpline(sketch, "E190", {"points": [v(-65.36, 90.06) * mm, v(-65.6, 88.8) * mm, v(-65.75, 82.37) * mm, v(-65.75, 73.8) * mm]});
            skFitSpline(sketch, "E191", {"points": [v(-67.84, 57.04) * mm, v(-70.71, 53.48) * mm, v(-72.89, 50.34) * mm, v(-75.08, 46.6) * mm]});
            skFitSpline(sketch, "E192", {"points": [v(-75.08, 46.6) * mm, v(-76.9, 43.53) * mm, v(-80.29, 36.6) * mm, v(-81.2, 34.1) * mm]});
            skFitSpline(sketch, "E193", {"points": [v(-81.2, 34.1) * mm, v(-81.46, 33.4) * mm, v(-81.8, 32.51) * mm, v(-81.96, 32.12) * mm]});
            skFitSpline(sketch, "E194", {"points": [v(-81.96, 32.12) * mm, v(-83.53, 28.37) * mm, v(-85.42, 21.06) * mm, v(-86.51, 14.48) * mm]});
            skFitSpline(sketch, "E195", {"points": [v(-86.51, 14.48) * mm, v(-87.43, 8.98) * mm, v(-87.42, -5.2) * mm, v(-86.5, -10.18) * mm]});
            skFitSpline(sketch, "E196", {"points": [v(-86.5, -10.18) * mm, v(-85.01, -18.32) * mm, v(-82.78, -26.1) * mm, v(-80.81, -30.06) * mm]});
            skFitSpline(sketch, "E197", {"points": [v(-80.81, -30.06) * mm, v(-80.25, -31.2) * mm, v(-79.8, -32.3) * mm, v(-79.8, -32.51) * mm]});
            skFitSpline(sketch, "E198", {"points": [v(-79.8, -32.51) * mm, v(-79.8, -32.73) * mm, v(-79.39, -33.5) * mm, v(-78.9, -34.23) * mm]});
            skFitSpline(sketch, "E199", {"points": [v(-78.9, -34.23) * mm, v(-78.4, -34.96) * mm, v(-78, -35.75) * mm, v(-78, -36) * mm]});
            skFitSpline(sketch, "E200", {"points": [v(-78, -36) * mm, v(-78, -36.25) * mm, v(-77.32, -37.55) * mm, v(-76.5, -38.89) * mm]});
            skFitSpline(sketch, "E201", {"points": [v(-76.5, -38.89) * mm, v(-75.67, -40.23) * mm, v(-74.78, -41.81) * mm, v(-74.5, -42.4) * mm]});
            skFitSpline(sketch, "E202", {"points": [v(-74.5, -42.4) * mm, v(-74.24, -43) * mm, v(-73.45, -44.21) * mm, v(-72.75, -45.1) * mm]});
            skFitSpline(sketch, "E203", {"points": [v(-72.75, -45.1) * mm, v(-72.06, -46) * mm, v(-71.4, -47) * mm, v(-71.28, -47.35) * mm]});
            skFitSpline(sketch, "E204", {"points": [v(-71.28, -47.35) * mm, v(-71.16, -47.7) * mm, v(-70.92, -47.98) * mm, v(-70.75, -47.98) * mm]});
            skFitSpline(sketch, "E205", {"points": [v(-70.75, -47.98) * mm, v(-70.57, -47.98) * mm, v(-70.43, -48.23) * mm, v(-70.43, -48.52) * mm]});
            skFitSpline(sketch, "E206", {"points": [v(-70.43, -48.52) * mm, v(-70.43, -48.82) * mm, v(-70.27, -49.06) * mm, v(-70.08, -49.06) * mm]});
            skFitSpline(sketch, "E207", {"points": [v(-70.08, -49.06) * mm, v(-69.89, -49.06) * mm, v(-69.49, -49.54) * mm, v(-69.19, -50.11) * mm]});
            skFitSpline(sketch, "E208", {"points": [v(-69.19, -50.11) * mm, v(-68.9, -50.69) * mm, v(-68.43, -51.37) * mm, v(-68.16, -51.64) * mm]});
            skFitSpline(sketch, "E209", {"points": [v(-68.16, -51.64) * mm, v(-67.9, -51.9) * mm, v(-67.37, -52.6) * mm, v(-66.99, -53.19) * mm]});
            skFitSpline(sketch, "E210", {"points": [v(-66.99, -53.19) * mm, v(-66.33, -54.18) * mm, v(-66.28, -55.22) * mm, v(-66.1, -69.75) * mm]});
            skFitSpline(sketch, "E211", {"points": [v(-66.1, -69.75) * mm, v(-65.92, -83.04) * mm, v(-65.8, -85.5) * mm, v(-65.28, -87.04) * mm]});
            skFitSpline(sketch, "E212", {"points": [v(-65.28, -87.04) * mm, v(-64.55, -89.2) * mm, v(-62.22, -92.65) * mm, v(-61.13, -93.2) * mm]});
            skFitSpline(sketch, "E213", {"points": [v(-61.13, -93.2) * mm, v(-60.7, -93.41) * mm, v(-60.02, -93.89) * mm, v(-59.62, -94.26) * mm]});
            skFitSpline(sketch, "E214", {"points": [v(-59.62, -94.26) * mm, v(-58.92, -94.89) * mm, v(-58.9, -94.9) * mm, v(-59.13, -94.27) * mm]});
            skFitSpline(sketch, "E215", {"points": [v(-59.13, -94.27) * mm, v(-59.33, -93.75) * mm, v(-59.24, -93.66) * mm, v(-58.7, -93.82) * mm]});
            skFitSpline(sketch, "E216", {"points": [v(-58.7, -93.82) * mm, v(-58.32, -93.93) * mm, v(-57.08, -94.21) * mm, v(-55.94, -94.46) * mm]});
            skFitSpline(sketch, "E217", {"points": [v(-55.94, -94.46) * mm, v(-54.8, -94.7) * mm, v(-53.87, -95.02) * mm, v(-53.87, -95.16) * mm]});
            skFitSpline(sketch, "E218", {"points": [v(-53.87, -95.16) * mm, v(-53.87, -95.53) * mm, v(-54.39, -95.51) * mm, v(-34.43, -95.8) * mm]});
            skFitSpline(sketch, "E219", {"points": [v(-34.43, -95.8) * mm, v(-14.07, -96.08) * mm, v(45.9, -96.03) * mm, v(50.61, -95.73) * mm]});
            skFitSpline(sketch, "E220", {"points": [v(-159.53, -91.73) * mm, v(-159.73, -91.66) * mm, v(-160.3, -91.52) * mm, v(-160.82, -91.4) * mm]});
            skFitSpline(sketch, "E221", {"points": [v(-160.82, -91.4) * mm, v(-162, -91.15) * mm, v(-162.6, -89.86) * mm, v(-162.6, -87.56) * mm]});
            skFitSpline(sketch, "E222", {"points": [v(-162.6, -87.56) * mm, v(-162.6, -83.13) * mm, v(-159.39, -80.38) * mm, v(-154.8, -80.85) * mm]});
            skFitSpline(sketch, "E223", {"points": [v(-154.8, -80.85) * mm, v(-151.08, -81.24) * mm, v(-148.65, -83.98) * mm, v(-148.58, -87.87) * mm]});
            skFitSpline(sketch, "E224", {"points": [v(-148.58, -87.87) * mm, v(-148.54, -90.01) * mm, v(-149.33, -91.4) * mm, v(-150.74, -91.68) * mm]});
            skFitSpline(sketch, "E225", {"points": [v(-150.74, -91.68) * mm, v(-151.9, -91.9) * mm, v(-158.87, -91.95) * mm, v(-159.53, -91.73) * mm]});
            skFitSpline(sketch, "E226", {"points": [v(-154.5, -90.47) * mm, v(-153.85, -90.22) * mm, v(-153.36, -90.24) * mm, v(-152.89, -90.54) * mm]});
            skFitSpline(sketch, "E227", {"points": [v(-152.89, -90.54) * mm, v(-152.35, -90.87) * mm, v(-151.98, -90.86) * mm, v(-151.19, -90.49) * mm]});
            skFitSpline(sketch, "E228", {"points": [v(-151.19, -90.49) * mm, v(-150.6, -90.2) * mm, v(-150.36, -89.94) * mm, v(-150.63, -89.85) * mm]});
            skFitSpline(sketch, "E229", {"points": [v(-150.63, -89.85) * mm, v(-150.93, -89.73) * mm, v(-150.8, -89.46) * mm, v(-150.22, -89) * mm]});
            skFitSpline(sketch, "E230", {"points": [v(-150.22, -89) * mm, v(-148.11, -87.34) * mm, v(-150.7, -82.8) * mm, v(-154.33, -81.82) * mm]});
            skFitSpline(sketch, "E231", {"points": [v(-154.33, -81.82) * mm, v(-157.3, -81.02) * mm, v(-160.6, -82.96) * mm, v(-161.53, -86.08) * mm]});
            skFitSpline(sketch, "E232", {"points": [v(-161.53, -86.08) * mm, v(-162.2, -88.28) * mm, v(-161.56, -89.37) * mm, v(-159.56, -89.44) * mm]});
            skFitSpline(sketch, "E233", {"points": [v(-159.71, -89.73) * mm, v(-161.57, -90) * mm, v(-161.09, -90.38) * mm, v(-158.63, -90.57) * mm]});
            skFitSpline(sketch, "E234", {"points": [v(-158.63, -90.57) * mm, v(-157.74, -90.64) * mm, v(-156.66, -90.73) * mm, v(-156.22, -90.76) * mm]});
            skFitSpline(sketch, "E235", {"points": [v(-156.22, -90.76) * mm, v(-155.8, -90.8) * mm, v(-155.02, -90.66) * mm, v(-154.5, -90.47) * mm]});
            skFitSpline(sketch, "E236", {"points": [v(138.7, 94.36) * mm, v(138.62, 94.44) * mm, v(138, 94.6) * mm, v(137.35, 94.7) * mm]});
            skFitSpline(sketch, "E237", {"points": [v(137.35, 94.7) * mm, v(135.22, 95.03) * mm, v(134.45, 96.79) * mm, v(135.05, 100) * mm]});
            skFitSpline(sketch, "E238", {"points": [v(135.05, 100) * mm, v(135.48, 102.33) * mm, v(136.45, 103.67) * mm, v(138.45, 104.7) * mm]});
            skFitSpline(sketch, "E239", {"points": [v(138.45, 104.7) * mm, v(140.19, 105.58) * mm, v(143.86, 105.58) * mm, v(145.39, 104.7) * mm]});
            skFitSpline(sketch, "E240", {"points": [v(145.39, 104.7) * mm, v(147.85, 103.25) * mm, v(149.46, 99.33) * mm, v(148.47, 97.17) * mm]});
            skFitSpline(sketch, "E241", {"points": [v(148.47, 97.17) * mm, v(147.39, 94.81) * mm, v(147.16, 94.44) * mm, v(146.73, 94.3) * mm]});
            skFitSpline(sketch, "E242", {"points": [v(146.73, 94.3) * mm, v(146.45, 94.2) * mm, v(146.57, 94.64) * mm, v(147.02, 95.41) * mm]});
            skFitSpline(sketch, "E243", {"points": [v(147.02, 95.41) * mm, v(147.44, 96.12) * mm, v(147.61, 96.76) * mm, v(147.42, 96.88) * mm]});
            skFitSpline(sketch, "E244", {"points": [v(147.42, 96.88) * mm, v(147.24, 97) * mm, v(147, 96.85) * mm, v(146.88, 96.55) * mm]});
            skFitSpline(sketch, "E245", {"points": [v(146.88, 96.55) * mm, v(146.76, 96.25) * mm, v(146.24, 96.02) * mm, v(145.67, 96.03) * mm]});
            skFitSpline(sketch, "E246", {"points": [v(145.67, 96.03) * mm, v(144.7, 96.04) * mm, v(144.7, 96.05) * mm, v(145.39, 96.58) * mm]});
            skFitSpline(sketch, "E247", {"points": [v(145.39, 96.58) * mm, v(145.79, 96.88) * mm, v(146.1, 97.32) * mm, v(146.1, 97.56) * mm]});
            skFitSpline(sketch, "E248", {"points": [v(146.1, 97.56) * mm, v(146.1, 97.8) * mm, v(146.47, 98.05) * mm, v(146.92, 98.11) * mm]});
            skFitSpline(sketch, "E249", {"points": [v(146.92, 98.11) * mm, v(147.5, 98.2) * mm, v(147.73, 98.47) * mm, v(147.73, 99.08) * mm]});
            skFitSpline(sketch, "E250", {"points": [v(147.73, 99.08) * mm, v(147.73, 99.55) * mm, v(147.57, 100.03) * mm, v(147.37, 100.16) * mm]});
            skFitSpline(sketch, "E251", {"points": [v(147.37, 100.16) * mm, v(147.17, 100.28) * mm, v(147, 100.64) * mm, v(147, 100.96) * mm]});
            skFitSpline(sketch, "E252", {"points": [v(147, 100.96) * mm, v(147, 101.27) * mm, v(146.77, 101.8) * mm, v(146.49, 102.1) * mm]});
            skFitSpline(sketch, "E253", {"points": [v(146.49, 102.1) * mm, v(146.2, 102.42) * mm, v(145.64, 103.03) * mm, v(145.25, 103.46) * mm]});
            skFitSpline(sketch, "E254", {"points": [v(145.25, 103.46) * mm, v(144.16, 104.67) * mm, v(141.63, 104.91) * mm, v(139.54, 104) * mm]});
            skFitSpline(sketch, "E255", {"points": [v(139.54, 104) * mm, v(137.36, 103.06) * mm, v(135.59, 100.78) * mm, v(136.18, 99.68) * mm]});
            skFitSpline(sketch, "E256", {"points": [v(136.18, 99.68) * mm, v(136.44, 99.2) * mm, v(136.45, 98.86) * mm, v(136.21, 98.72) * mm]});
            skFitSpline(sketch, "E257", {"points": [v(136.21, 98.72) * mm, v(135.62, 98.35) * mm, v(135.8, 97.62) * mm, v(136.73, 96.6) * mm]});
            skFitSpline(sketch, "E258", {"points": [v(136.73, 96.6) * mm, v(137.56, 95.71) * mm, v(139.03, 95.23) * mm, v(138.55, 96.02) * mm]});
            skFitSpline(sketch, "E259", {"points": [v(138.55, 96.02) * mm, v(138.43, 96.21) * mm, v(138.5, 96.38) * mm, v(138.7, 96.38) * mm]});
            skFitSpline(sketch, "E260", {"points": [v(138.7, 96.38) * mm, v(138.92, 96.38) * mm, v(139.09, 96.15) * mm, v(139.09, 95.87) * mm]});
            skFitSpline(sketch, "E261", {"points": [v(139.09, 95.87) * mm, v(139.09, 94.98) * mm, v(141.2, 94.83) * mm, v(144.26, 95.52) * mm]});
            skFitSpline(sketch, "E262", {"points": [v(144.26, 95.52) * mm, v(145.22, 95.74) * mm, v(145.26, 95.7) * mm, v(144.88, 94.98) * mm]});
            skFitSpline(sketch, "E263", {"points": [v(144.88, 94.98) * mm, v(144.5, 94.3) * mm, v(144.16, 94.22) * mm, v(141.66, 94.22) * mm]});
            skFitSpline(sketch, "E264", {"points": [v(141.66, 94.22) * mm, v(140.11, 94.22) * mm, v(138.78, 94.28) * mm, v(138.7, 94.36) * mm]});
            skFitSpline(sketch, "E265", {"points": [v(-146.3, 95.53) * mm, v(-148.48, 96) * mm, v(-148.8, 100.73) * mm, v(-146.82, 103.18) * mm]});
            skFitSpline(sketch, "E266", {"points": [v(-146.82, 103.18) * mm, v(-145.16, 105.23) * mm, v(-143.7, 105.91) * mm, v(-140.93, 105.91) * mm]});
            skFitSpline(sketch, "E267", {"points": [v(-140.93, 105.91) * mm, v(-138.85, 105.92) * mm, v(-138.33, 105.77) * mm, v(-136.97, 104.83) * mm]});
            skFitSpline(sketch, "E268", {"points": [v(-136.97, 104.83) * mm, v(-136.11, 104.23) * mm, v(-135.13, 103.17) * mm, v(-134.78, 102.49) * mm]});
            skFitSpline(sketch, "E269", {"points": [v(-134.78, 102.49) * mm, v(-133.9, 100.74) * mm, v(-133.93, 97.44) * mm, v(-134.84, 96.33) * mm]});
            skFitSpline(sketch, "E270", {"points": [v(-134.84, 96.33) * mm, v(-135.5, 95.51) * mm, v(-135.74, 95.47) * mm, v(-140.5, 95.42) * mm]});
            skFitSpline(sketch, "E271", {"points": [v(-140.5, 95.42) * mm, v(-143.25, 95.39) * mm, v(-145.86, 95.44) * mm, v(-146.3, 95.53) * mm]});
            skFitSpline(sketch, "E272", {"points": [v(-139.33, 96.39) * mm, v(-138.65, 96.65) * mm, v(-138.28, 96.65) * mm, v(-138.12, 96.39) * mm]});
            skFitSpline(sketch, "E273", {"points": [v(-138.12, 96.39) * mm, v(-137.97, 96.14) * mm, v(-137.66, 96.19) * mm, v(-137.2, 96.52) * mm]});
            skFitSpline(sketch, "E274", {"points": [v(-137.2, 96.52) * mm, v(-136.83, 96.8) * mm, v(-136.31, 96.93) * mm, v(-136.06, 96.84) * mm]});
            skFitSpline(sketch, "E275", {"points": [v(-136.06, 96.84) * mm, v(-135.8, 96.74) * mm, v(-135.6, 96.84) * mm, v(-135.6, 97.06) * mm]});
            skFitSpline(sketch, "E276", {"points": [v(-135.6, 97.06) * mm, v(-135.6, 97.28) * mm, v(-135.95, 97.47) * mm, v(-136.4, 97.5) * mm]});
            skFitSpline(sketch, "E277", {"points": [v(-136.4, 97.5) * mm, v(-137.13, 97.53) * mm, v(-137.14, 97.56) * mm, v(-136.5, 97.71) * mm]});
            skFitSpline(sketch, "E278", {"points": [v(-136.5, 97.71) * mm, v(-135.5, 97.95) * mm, v(-135.23, 98.26) * mm, v(-135.03, 99.38) * mm]});
            skFitSpline(sketch, "E279", {"points": [v(-135.03, 99.38) * mm, v(-134.78, 100.73) * mm, v(-136.05, 103.01) * mm, v(-137.65, 104.1) * mm]});
            skFitSpline(sketch, "E280", {"points": [v(-137.65, 104.1) * mm, v(-138.4, 104.6) * mm, v(-139.16, 105.01) * mm, v(-139.36, 105) * mm]});
            skFitSpline(sketch, "E281", {"points": [v(-139.36, 105) * mm, v(-139.57, 105) * mm, v(-139.49, 104.85) * mm, v(-139.2, 104.66) * mm]});
            skFitSpline(sketch, "E282", {"points": [v(-139.2, 104.66) * mm, v(-138.72, 104.35) * mm, v(-138.73, 104.3) * mm, v(-139.26, 104.3) * mm]});
            skFitSpline(sketch, "E283", {"points": [v(-139.26, 104.3) * mm, v(-139.6, 104.3) * mm, v(-139.97, 104.46) * mm, v(-140.1, 104.66) * mm]});
            skFitSpline(sketch, "E284", {"points": [v(-140.1, 104.66) * mm, v(-140.21, 104.85) * mm, v(-140.8, 105.02) * mm, v(-141.38, 105.02) * mm]});
            skFitSpline(sketch, "E285", {"points": [v(-141.38, 105.02) * mm, v(-144.34, 105.02) * mm, v(-147.11, 102.34) * mm, v(-147.11, 99.49) * mm]});
            skFitSpline(sketch, "E286", {"points": [v(-147.11, 99.49) * mm, v(-147.11, 98.36) * mm, v(-146.99, 98.2) * mm, v(-145.94, 97.97) * mm]});
            skFitSpline(sketch, "E287", {"points": [v(-145.94, 97.97) * mm, v(-144.93, 97.75) * mm, v(-144.87, 97.68) * mm, v(-145.5, 97.45) * mm]});
            skFitSpline(sketch, "E288", {"points": [v(-145.5, 97.45) * mm, v(-145.89, 97.3) * mm, v(-146.37, 97.28) * mm, v(-146.57, 97.39) * mm]});
            skFitSpline(sketch, "E289", {"points": [v(-146.57, 97.39) * mm, v(-146.77, 97.5) * mm, v(-146.72, 97.34) * mm, v(-146.47, 97.02) * mm]});
            skFitSpline(sketch, "E290", {"points": [v(-146.47, 97.02) * mm, v(-146.16, 96.65) * mm, v(-145.5, 96.48) * mm, v(-144.49, 96.52) * mm]});
            skFitSpline(sketch, "E291", {"points": [v(-144.49, 96.52) * mm, v(-143.65, 96.56) * mm, v(-142.57, 96.47) * mm, v(-142.07, 96.33) * mm]});
            skFitSpline(sketch, "E292", {"points": [v(-142.07, 96.33) * mm, v(-140.77, 95.96) * mm, v(-140.43, 95.97) * mm, v(-139.33, 96.39) * mm]});
            skFitSpline(sketch, "E293", {"points": [v(139.99, 95.66) * mm, v(139.87, 95.85) * mm, v(139.94, 96.02) * mm, v(140.15, 96.02) * mm]});
            skFitSpline(sketch, "E294", {"points": [v(140.15, 96.02) * mm, v(140.36, 96.02) * mm, v(140.53, 95.85) * mm, v(140.53, 95.66) * mm]});
            skFitSpline(sketch, "E295", {"points": [v(140.53, 95.66) * mm, v(140.53, 95.46) * mm, v(140.46, 95.3) * mm, v(140.37, 95.3) * mm]});
            skFitSpline(sketch, "E296", {"points": [v(140.37, 95.3) * mm, v(140.28, 95.3) * mm, v(140.11, 95.46) * mm, v(139.99, 95.66) * mm]});
            skSolve(sketch);
        }
        {
            var Q0;
            Q0=qCreatedBy(makeId("Top.planeOp"),FACE);
            var sketch = newSketch(context, id + "F1", { "sketchPlane" : qUnion([Q0])});
            skPoint(sketch, "E297.0", {"position": v(-172.6, 139.33) * mm});
            skPoint(sketch, "E298.0", {"position": v(-218.57, -20.44) * mm});
            skPoint(sketch, "E299.0", {"position": v(219.39, -13.14) * mm});
            skCircle(sketch, "E300", {"center": v(0.08, 3.15) * mm, "radius": 219.92 * mm});
            skCircle(sketch, "E301", {"center": v(0.08, 3.15) * mm, "radius": 85 * mm});
            skCircle(sketch, "E302", {"center": v(0.08, 3.15) * mm, "radius": 234.92 * mm});
            skPoint(sketch, "E303.0", {"position": v(-134.78, 102.49) * mm});
            skPoint(sketch, "E304.0", {"position": v(-146.82, 103.18) * mm});
            skPoint(sketch, "E305.0", {"position": v(-134.84, 96.33) * mm});
            skCircle(sketch, "E306", {"center": v(-141, 99.46) * mm, "radius": 6.91 * mm});
            skPoint(sketch, "E307.0", {"position": v(-154.8, -80.85) * mm});
            skPoint(sketch, "E308.0", {"position": v(-148.58, -87.87) * mm});
            skPoint(sketch, "E309.0", {"position": v(-162.6, -87.56) * mm});
            skCircle(sketch, "E310", {"center": v(-155.59, -87.82) * mm, "radius": 7 * mm});
            skPoint(sketch, "E311.0", {"position": v(148.44, -91.5) * mm});
            skPoint(sketch, "E312.0", {"position": v(136.96, -88.54) * mm});
            skPoint(sketch, "E313.0", {"position": v(147.23, -97.78) * mm});
            skCircle(sketch, "E314", {"center": v(141.81, -93.47) * mm, "radius": 6.92 * mm});
            skPoint(sketch, "E315.0", {"position": v(138.45, 104.7) * mm});
            skPoint(sketch, "E316.0", {"position": v(145.39, 104.7) * mm});
            skPoint(sketch, "E317.0", {"position": v(135.05, 100) * mm});
            skCircle(sketch, "E318", {"center": v(142.4, 98.26) * mm, "radius": 7.55 * mm});
            skPoint(sketch, "E318.first.point", {"position": v(146.33, 104.7) * mm});
            skLineSegment(sketch, "E319", {"start": v(-156.48, -172) * mm, "end": v(156.64, -172) * mm});
            skLineSegment(sketch, "E320", {"start": v(0.08, 3.15) * mm, "end": v(-266.63, 3.15) * mm, "construction": true});
            skLineSegment(sketch, "E321.MirrorCS", {"start": v(-156.48, 178.3) * mm, "end": v(156.64, 178.3) * mm});
            skSolve(sketch);
        }
        {
            var Q0;
            {var subQ0=sQuery(id+"F1.wireOp",EDGE,"E321.MirrorCS");var subQ1=sQuery(id+"F1.wireOp",EDGE,"E300");var subQ2=makeQuery(id+"F1.imprint","INTERSECT",VERTEX,{"disambiguationData":[OD(0.0)],"derivedFrom":[subQ1,subQ0]});Q0=makeQuery(id+"F1.imprint","IMPRINT",FACE,{"disambiguationData":[TD([[makeQuery(id+"F1.imprint","IMPRINT",EDGE,{"disambiguationData":[TD([[subQ2,-1.0]])],"derivedFrom":subQ1}),-1.0]])]});}
            var Q1;
            {var subQ0=sQuery(id+"F1.wireOp",EDGE,"E321.MirrorCS");var subQ1=sQuery(id+"F1.wireOp",EDGE,"E300");var subQ2=makeQuery(id+"F1.imprint","INTERSECT",VERTEX,{"disambiguationData":[OD(1.0)],"derivedFrom":[subQ1,subQ0]});Q1=makeQuery(id+"F1.imprint","IMPRINT",FACE,{"disambiguationData":[TD([[makeQuery(id+"F1.imprint","IMPRINT",EDGE,{"disambiguationData":[TD([[subQ2,1.0]])],"derivedFrom":subQ1}),-1.0]])]});}
            var Q2;
            Q2=makeQuery(id+"F1.imprint","IMPRINT",FACE,{"disambiguationData":[TD([[makeQuery(id+"F1.imprint","IMPRINT",EDGE,{"derivedFrom":sQuery(id+"F1.wireOp",EDGE,"E301")}),-1.0]])]});
            extrude(context, id + "F2", {"entities" : qUnion([Q0, Q1, Q2]), "depth" : 3 * mm, "offsetDistance" : 25 * mm});
        }
    });
